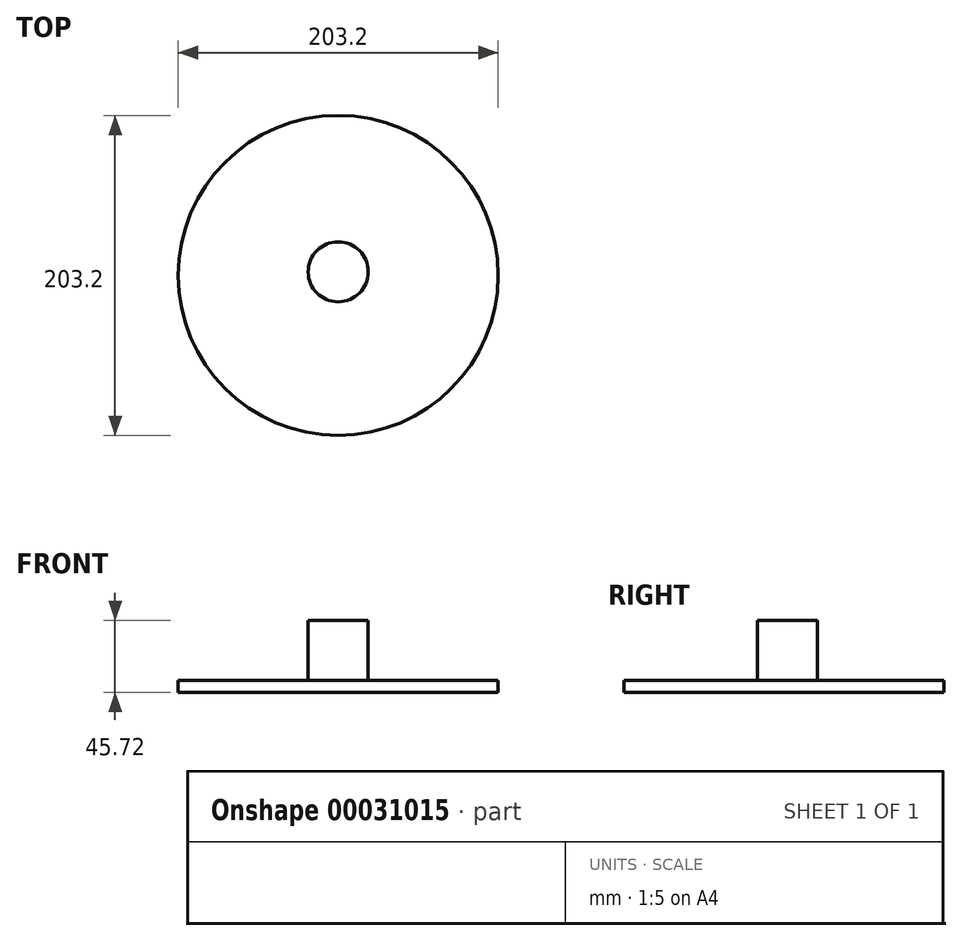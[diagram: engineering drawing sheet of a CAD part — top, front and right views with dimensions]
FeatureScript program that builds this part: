
annotation { "Feature Type Name" : "Feature", "Feature Type Description" : "" }
export const myFeature = defineFeature(function(context is Context, id is Id, definition is map)
    precondition{}
    {
        {
            var Q0;
            Q0=qCreatedBy(makeId("Top.planeOp"),FACE);
            var sketch = newSketch(context, id + "F0", { "sketchPlane" : qUnion([Q0])});
            skCircle(sketch, "E0", {"center": v(0, 0) * mm, "radius": 101.6 * mm});
            skCircle(sketch, "E1", {"center": v(0, 0) * mm, "radius": 72.77 * mm});
            skCircle(sketch, "E2", {"center": v(0, 2.3) * mm, "radius": 19.05 * mm});
            skSolve(sketch);
        }
        {
            var Q0;
            Q0=makeQuery(id+"F0.imprint","IMPRINT",FACE,{"disambiguationData":[TD([[makeQuery(id+"F0.imprint","IMPRINT",EDGE,{"derivedFrom":sQuery(id+"F0.wireOp",EDGE,"E2")}),1.0]])]});
            extrude(context, id + "F1", {"entities" : qUnion([Q0]), "depth" : 45.72 * mm});
        }
        {
            var Q0;
            Q0=makeQuery(id+"F0.imprint","IMPRINT",FACE,{"disambiguationData":[TD([[makeQuery(id+"F0.imprint","IMPRINT",EDGE,{"derivedFrom":sQuery(id+"F0.wireOp",EDGE,"E0")}),1.0]])]});
            var Q1;
            Q1=makeQuery(id+"F0.imprint","IMPRINT",FACE,{"disambiguationData":[TD([[makeQuery(id+"F0.imprint","IMPRINT",EDGE,{"derivedFrom":sQuery(id+"F0.wireOp",EDGE,"E1")}),1.0]])]});
            extrude(context, id + "F2", {"entities" : qUnion([Q0, Q1]), "operationType" : NewBodyOperationType.ADD, "depth" : 7.62 * mm});
        }
    });
